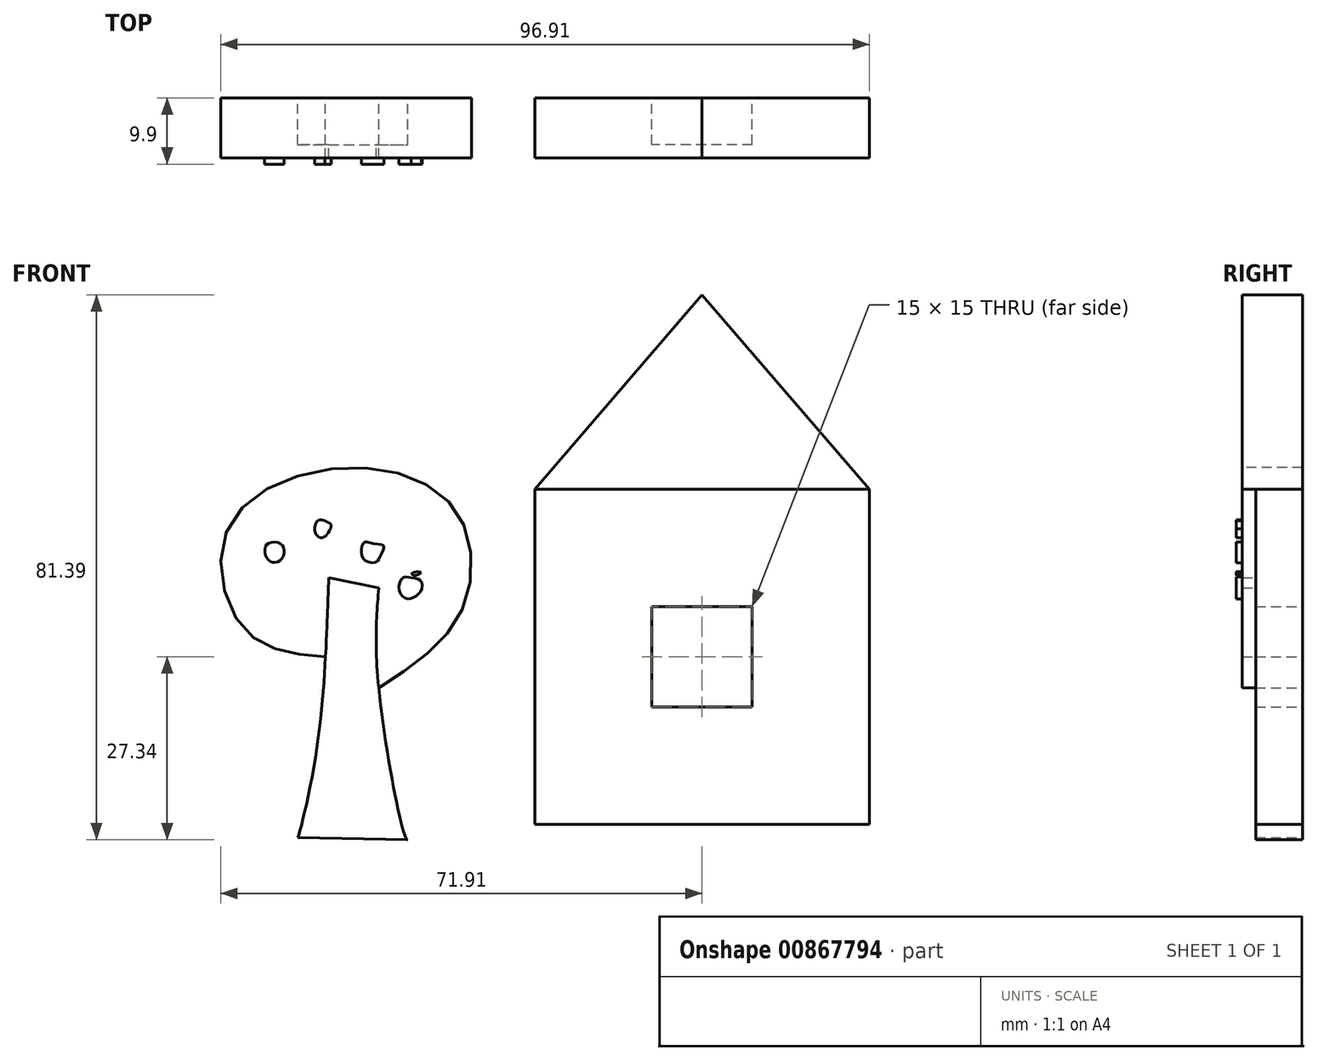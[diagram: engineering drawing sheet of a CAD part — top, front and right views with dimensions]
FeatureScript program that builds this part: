
annotation { "Feature Type Name" : "Feature", "Feature Type Description" : "" }
export const myFeature = defineFeature(function(context is Context, id is Id, definition is map)
    precondition{}
    {
        {
            var Q0;
            Q0=qCreatedBy(makeId("Front.planeOp"),FACE);
            var sketch = newSketch(context, id + "F0", { "sketchPlane" : qUnion([Q0])});
            skLineSegment(sketch, "E0.bottom", {"start": v(25, 25) * mm, "end": v(-25, 25) * mm});
            skLineSegment(sketch, "E0.top", {"start": v(25, -25) * mm, "end": v(-25, -25) * mm});
            skLineSegment(sketch, "E0.left", {"start": v(25, 25) * mm, "end": v(25, -25) * mm});
            skLineSegment(sketch, "E0.right", {"start": v(-25, 25) * mm, "end": v(-25, -25) * mm});
            skPoint(sketch, "E0.middle", {"position": v(0, 0) * mm});
            skLineSegment(sketch, "E1", {"start": v(-25, 25) * mm, "end": v(0, 54.05) * mm});
            skLineSegment(sketch, "E2", {"start": v(0, 54.05) * mm, "end": v(25, 25) * mm});
            skLineSegment(sketch, "E3.bottom", {"start": v(7.5, 7.5) * mm, "end": v(-7.5, 7.5) * mm});
            skLineSegment(sketch, "E3.top", {"start": v(7.5, -7.5) * mm, "end": v(-7.5, -7.5) * mm});
            skLineSegment(sketch, "E3.left", {"start": v(7.5, 7.5) * mm, "end": v(7.5, -7.5) * mm});
            skLineSegment(sketch, "E3.right", {"start": v(-7.5, 7.5) * mm, "end": v(-7.5, -7.5) * mm});
            skFitSpline(sketch, "E4", {"points": [v(-55.76, 11.8) * mm, v(-56.07, 3.73) * mm, v(-57.94, -16.15) * mm, v(-60.42, -27.03) * mm, v(-60.42, -26.72) * mm], "startDerivative": vector(-0.97, -28.3) * mm, "endDerivative": vector(0.71, 9.3) * mm});
            skFitSpline(sketch, "E5", {"points": [v(-48.3, 10.25) * mm, v(-48.3, -4.66) * mm, v(-44.27, -27.03) * mm, v(-43.96, -27.34) * mm], "startDerivative": vector(-2.4, -29.53) * mm, "endDerivative": vector(3.96, -1.48) * mm});
            skFitSpline(sketch, "E6", {"points": [v(-56.26, 0) * mm, v(-68.03, 3.73) * mm, v(-70.86, 19.12) * mm, v(-53.59, 28.19) * mm, v(-36.87, 21.95) * mm, v(-36.02, 6.66) * mm, v(-48.3, -4.66) * mm], "startDerivative": vector(-90.02, 6.7) * mm, "endDerivative": vector(-87.79, -56.4) * mm});
            skFitSpline(sketch, "E7", {"points": [v(-62.65, 16.57) * mm, v(-64.96, 16.8) * mm, v(-64.93, 14.62) * mm, v(-63.15, 14.27) * mm, v(-62.65, 16.57) * mm]});
            skFitSpline(sketch, "E8", {"points": [v(-63.86, 17.12) * mm, v(-63.47, 18.7) * mm, v(-63.41, 18.67) * mm], "startDerivative": vector(0.51, 2.76) * mm, "endDerivative": vector(0.34, -0.35) * mm});
            skFitSpline(sketch, "E9", {"points": [v(-56.36, 20.34) * mm, v(-57.49, 20.25) * mm, v(-57.76, 18.5) * mm, v(-56.74, 17.75) * mm, v(-55.5, 19.12) * mm], "startDerivative": vector(-5.83, 1.14) * mm, "endDerivative": vector(4.2, 6.93) * mm});
            skFitSpline(sketch, "E10", {"points": [v(-55.5, 19.12) * mm, v(-55.5, 19.83) * mm, v(-56.36, 20.34) * mm, v(-56.36, 21.35) * mm], "startDerivative": vector(0.76, 2.74) * mm, "endDerivative": vector(0.84, 3.32) * mm});
            skFitSpline(sketch, "E11", {"points": [v(-49.03, 16.89) * mm, v(-50.5, 17.06) * mm, v(-50.88, 15.84) * mm, v(-50.4, 14.44) * mm, v(-48.73, 14.12) * mm, v(-48, 15.16) * mm, v(-47.57, 16.57) * mm, v(-49.03, 16.89) * mm]});
            skFitSpline(sketch, "E12", {"points": [v(-49.03, 16.89) * mm, v(-48.3, 18.52) * mm], "startDerivative": vector(0.73, 1.64) * mm, "endDerivative": vector(0.73, 1.64) * mm});
            skFitSpline(sketch, "E13", {"points": [v(-43.43, 11.8) * mm, v(-44.7, 11.8) * mm, v(-45.27, 10.09) * mm, v(-44.24, 8.7) * mm, v(-42.97, 8.92) * mm, v(-41.98, 9.94) * mm, v(-42.01, 11.36) * mm, v(-43.43, 11.8) * mm]});
            skFitSpline(sketch, "E14", {"points": [v(-43.43, 11.8) * mm, v(-43.43, 12.39) * mm, v(-43.07, 13.17) * mm, v(-43, 13.13) * mm], "startDerivative": vector(-0.22, 1.28) * mm, "endDerivative": vector(0.44, -0.5) * mm});
            skFitSpline(sketch, "E15", {"points": [v(-43.43, 12.39) * mm, v(-42.86, 12.64) * mm, v(-42.15, 12.64) * mm, v(-41.96, 12.55) * mm], "startDerivative": vector(1.36, 0.8) * mm, "endDerivative": vector(0.7, -0.44) * mm});
            skFitSpline(sketch, "E16", {"points": [v(-43.43, 12.39) * mm, v(-42.86, 12.12) * mm, v(-41.96, 12.55) * mm], "startDerivative": vector(1.2, -0.9) * mm, "endDerivative": vector(1.71, 1.14) * mm});
            skLineSegment(sketch, "E17", {"start": v(29.32, -22.52) * mm, "end": v(29.32, 0) * mm});
            skLineSegment(sketch, "E18", {"start": v(29.32, 0) * mm, "end": v(35.55, 0) * mm});
            skLineSegment(sketch, "E19", {"start": v(35.55, 0) * mm, "end": v(35.55, -23.09) * mm});
            skLineSegment(sketch, "E20", {"start": v(40.65, -22.52) * mm, "end": v(40.65, 0) * mm});
            skLineSegment(sketch, "E21", {"start": v(40.65, 0) * mm, "end": v(48.3, 0) * mm});
            skLineSegment(sketch, "E22", {"start": v(48.3, 0) * mm, "end": v(48.3, -23.37) * mm});
            skLineSegment(sketch, "E23", {"start": v(54.25, -20.54) * mm, "end": v(54.25, 0) * mm});
            skLineSegment(sketch, "E24", {"start": v(54.25, 0) * mm, "end": v(60.48, -1) * mm});
            skLineSegment(sketch, "E25", {"start": v(60.48, -1) * mm, "end": v(60.48, -23.37) * mm});
            skLineSegment(sketch, "E26", {"start": v(60.48, -5.52) * mm, "end": v(29.32, -5.52) * mm});
            skLineSegment(sketch, "E27", {"start": v(29.32, -5.52) * mm, "end": v(25, -5.52) * mm});
            skLineSegment(sketch, "E28", {"start": v(25, -5.52) * mm, "end": v(25, -13.46) * mm});
            skLineSegment(sketch, "E29", {"start": v(25, -13.46) * mm, "end": v(60.48, -13.46) * mm});
            skLineSegment(sketch, "E30", {"start": v(-60.42, -27.03) * mm, "end": v(-43.96, -27.34) * mm});
            skLineSegment(sketch, "E31", {"start": v(29.32, -22.52) * mm, "end": v(35.55, -23.09) * mm});
            skLineSegment(sketch, "E32", {"start": v(40.65, -22.52) * mm, "end": v(48.3, -23.37) * mm});
            skLineSegment(sketch, "E33", {"start": v(54.25, -20.54) * mm, "end": v(60.48, -23.37) * mm});
            skLineSegment(sketch, "E34", {"start": v(-55.76, 11.8) * mm, "end": v(-48.3, 10.25) * mm});
            skSolve(sketch);
        }
        {
            var Q0;
            {var subQ3=sQuery(id+"F0.wireOp",EDGE,"E0.bottom");Q0=makeQuery(id+"F0.imprint","IMPRINT",FACE,{"disambiguationData":[TD([[makeQuery(id+"F0.imprint","IMPRINT",EDGE,{"derivedFrom":subQ3}),1.0]])]});}
            extrude(context, id + "F1", {"entities" : qUnion([Q0]), "depth" : 7 * mm, "offsetDistance" : 25 * mm});
        }
        {
            var Q0;
            Q0=makeQuery(id+"F0.imprint","IMPRINT",FACE,{"disambiguationData":[TD([[makeQuery(id+"F0.imprint","IMPRINT",EDGE,{"derivedFrom":sQuery(id+"F0.wireOp",EDGE,"E0.bottom")}),-1.0]])]});
            extrude(context, id + "F2", {"entities" : qUnion([Q0]), "operationType" : NewBodyOperationType.ADD, "depth" : 9 * mm, "offsetDistance" : 25 * mm});
        }
        {
            var Q0;
            {var subQ5=sQuery(id+"F0.wireOp",EDGE,"E34");Q0=makeQuery(id+"F0.imprint","IMPRINT",FACE,{"disambiguationData":[TD([[makeQuery(id+"F0.imprint","IMPRINT",EDGE,{"derivedFrom":subQ5}),-1.0]])]});}
            extrude(context, id + "F3", {"entities" : qUnion([Q0]), "depth" : 7 * mm, "offsetDistance" : 25 * mm});
        }
        {
            var Q0;
            {var subQ4=sQuery(id+"F0.wireOp",EDGE,"E6");Q0=makeQuery(id+"F0.imprint","IMPRINT",FACE,{"disambiguationData":[TD([[makeQuery(id+"F0.imprint","IMPRINT",EDGE,{"derivedFrom":subQ4}),-1.0]])]});}
            extrude(context, id + "F4", {"entities" : qUnion([Q0]), "operationType" : NewBodyOperationType.ADD, "depth" : 9 * mm, "offsetDistance" : 25 * mm});
        }
        {
            var Q0;
            Q0=makeQuery(id+"F0.imprint","IMPRINT",FACE,{"disambiguationData":[TD([[makeQuery(id+"F0.imprint","IMPRINT",EDGE,{"derivedFrom":sQuery(id+"F0.wireOp",EDGE,"E13")}),1.0]])]});
            var Q1;
            Q1=makeQuery(id+"F0.imprint","IMPRINT",FACE,{"disambiguationData":[TD([[makeQuery(id+"F0.imprint","IMPRINT",EDGE,{"derivedFrom":sQuery(id+"F0.wireOp",EDGE,"E11")}),1.0]])]});
            var Q2;
            {var subQ0=sQuery(id+"F0.wireOp",EDGE,"E9");Q2=makeQuery(id+"F0.imprint","IMPRINT",FACE,{"disambiguationData":[TD([[makeQuery(id+"F0.imprint","IMPRINT",EDGE,{"derivedFrom":subQ0}),1.0]])]});}
            var Q3;
            Q3=makeQuery(id+"F0.imprint","IMPRINT",FACE,{"disambiguationData":[TD([[makeQuery(id+"F0.imprint","IMPRINT",EDGE,{"derivedFrom":sQuery(id+"F0.wireOp",EDGE,"E7")}),1.0]])]});
            var Q4;
            Q4=makeQuery(id+"F0.imprint","IMPRINT",FACE,{"disambiguationData":[TD([[makeQuery(id+"F0.imprint","IMPRINT",EDGE,{"derivedFrom":sQuery(id+"F0.wireOp",EDGE,"E15")}),-1.0]])]});
            extrude(context, id + "F5", {"entities" : qUnion([Q0, Q1, Q2, Q3, Q4]), "operationType" : NewBodyOperationType.ADD, "depth" : 9.9 * mm, "offsetDistance" : 25 * mm});
        }
    });
